# Revit family: IEK_Выключатель_ОткрытойУстановки_10А двухклавишный IP54_AQUATIC
name_source: partatom
category: Выключатели
units: mm (PartAtom-declared; Revit-internal decimal feet)

## family parameters
Всегда вертикально = Да
На основе рабочей плоскости = Нет
Общий = Нет
При загрузке вырезать с полостями = Нет
Размер круглого соединителя = Использовать диаметр
Сохранять ориентацию аннотаций = Да
Тип детали = Переключатель
Точка расчета площади = Нет

## types (1)
- ВС-20-2-0-А
    ADSK_URL страницы изделия = https://www.iek.ru
    ADSK_Версия Revit = 2019
    ADSK_Версия семейства = 1.0
    ADSK_Группирование = III ЭЛЕКТРОУСТАНОВОЧНЫЕ И ЭЛЕКТРОМОНТАЖНЫЕ ИЗДЕЛИЯ
    ADSK_Единица измерения = шт
    ADSK_Завод-изготовитель = IEK
    ADSK_Код изделия = EVA20-K03-10-54
    ADSK_Количество фаз = 1
    ADSK_Количество фаз числовое = 1
    ADSK_Марка = AQUATIC
    ADSK_Масса = 0.114
    ADSK_Материал = Окраска - RAL 7035
    ADSK_Материал наименование = Пластик
    ADSK_Наименование = Выключатель 2-клавишный для открытой установки ВС-20-2-0-А 10А IP54 AQUATIC IEK
    ADSK_Напряжение = 220 В
    IEK_URL = https://www.iek.ru
    IEK_Описание = Серия электроустановочных изделий AQUATIC IEK с повышенной степенью защиты IP54 предназначена для организации электроснабжения в условиях высокой влажности, в пыльных помещениях, мастерских, гаражах, а также на улице при установке под навесом, защищающем от прямого попадания осадков. Серия AQUATIC IEK продумана до мельчайших деталей для удобства и безопасного использования.
    IEK_Цена за единицу = 261.62
    KSI_CMa_Строительные материалы = 01.7.14.03
    KSI_CPr_Строительные изделия = 20.4.01
    Высота = 77 мм
    Глубина = 50 мм
    Изготовитель = IEK
    Степень защиты = IP54
    Тип монтажа = Поверхность монтажа (открытая установка)
    Ширина = 72 мм
